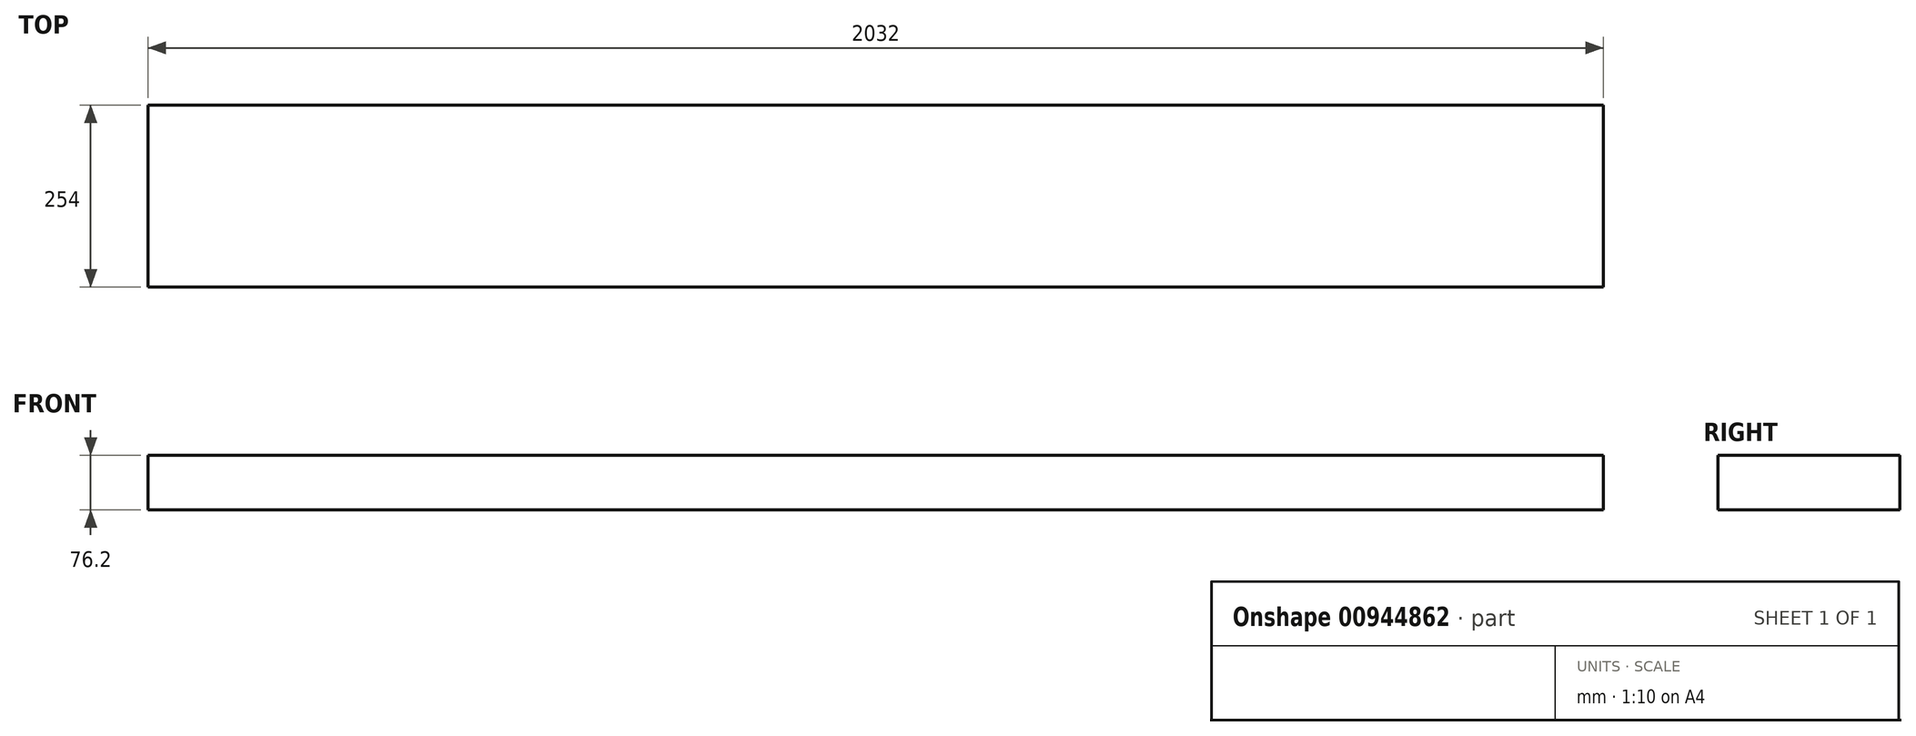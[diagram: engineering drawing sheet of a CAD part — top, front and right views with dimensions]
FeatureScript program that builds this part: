
annotation { "Feature Type Name" : "Feature", "Feature Type Description" : "" }
export const myFeature = defineFeature(function(context is Context, id is Id, definition is map)
    precondition{}
    {
        {
            var Q0;
            Q0=qCreatedBy(makeId("Top.planeOp"),FACE);
            var sketch = newSketch(context, id + "F0", { "sketchPlane" : qUnion([Q0])});
            skLineSegment(sketch, "E0.bottom", {"start": v(1414.94, 0) * mm, "end": v(-617.06, 0) * mm});
            skLineSegment(sketch, "E0.top", {"start": v(1414.94, 254) * mm, "end": v(-617.06, 254) * mm});
            skLineSegment(sketch, "E0.left", {"start": v(1414.94, 0) * mm, "end": v(1414.94, 254) * mm});
            skLineSegment(sketch, "E0.right", {"start": v(-617.06, 0) * mm, "end": v(-617.06, 254) * mm});
            skSolve(sketch);
        }
        {
            var Q0;
            Q0 = qSketchRegion(id + "F0", true);
            extrude(context, id + "F1", {"entities" : qUnion([Q0]), "depth" : 76.2 * mm, "offsetDistance" : 25.4 * mm});
        }
    });
